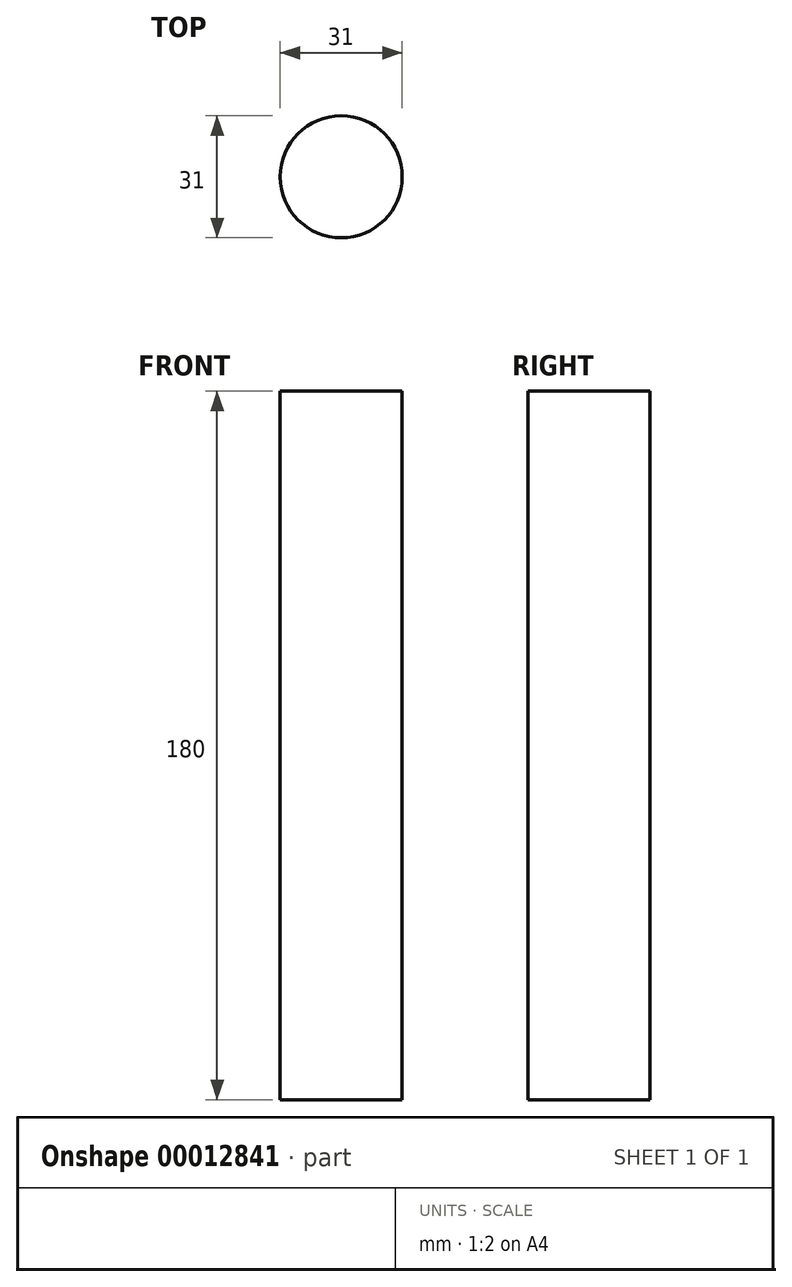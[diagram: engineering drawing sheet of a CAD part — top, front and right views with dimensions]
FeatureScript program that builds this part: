
annotation { "Feature Type Name" : "Feature", "Feature Type Description" : "" }
export const myFeature = defineFeature(function(context is Context, id is Id, definition is map)
    precondition{}
    {
        {
            var Q0;
            Q0=qCreatedBy(makeId("Top.planeOp"),FACE);
            var sketch = newSketch(context, id + "F0", { "sketchPlane" : qUnion([Q0])});
            skCircle(sketch, "E0", {"center": v(0, 0) * mm, "radius": 15.5 * mm});
            skSolve(sketch);
        }
        {
            var Q0;
            Q0=makeQuery(id+"F0.imprint","IMPRINT",FACE,{"disambiguationData":[TD([[makeQuery(id+"F0.imprint","IMPRINT",EDGE,{"derivedFrom":sQuery(id+"F0.wireOp",EDGE,"E0")}),1.0]])]});
            extrude(context, id + "F1", {"entities" : qUnion([Q0]), "depth" : 180 * mm});
        }
    });
